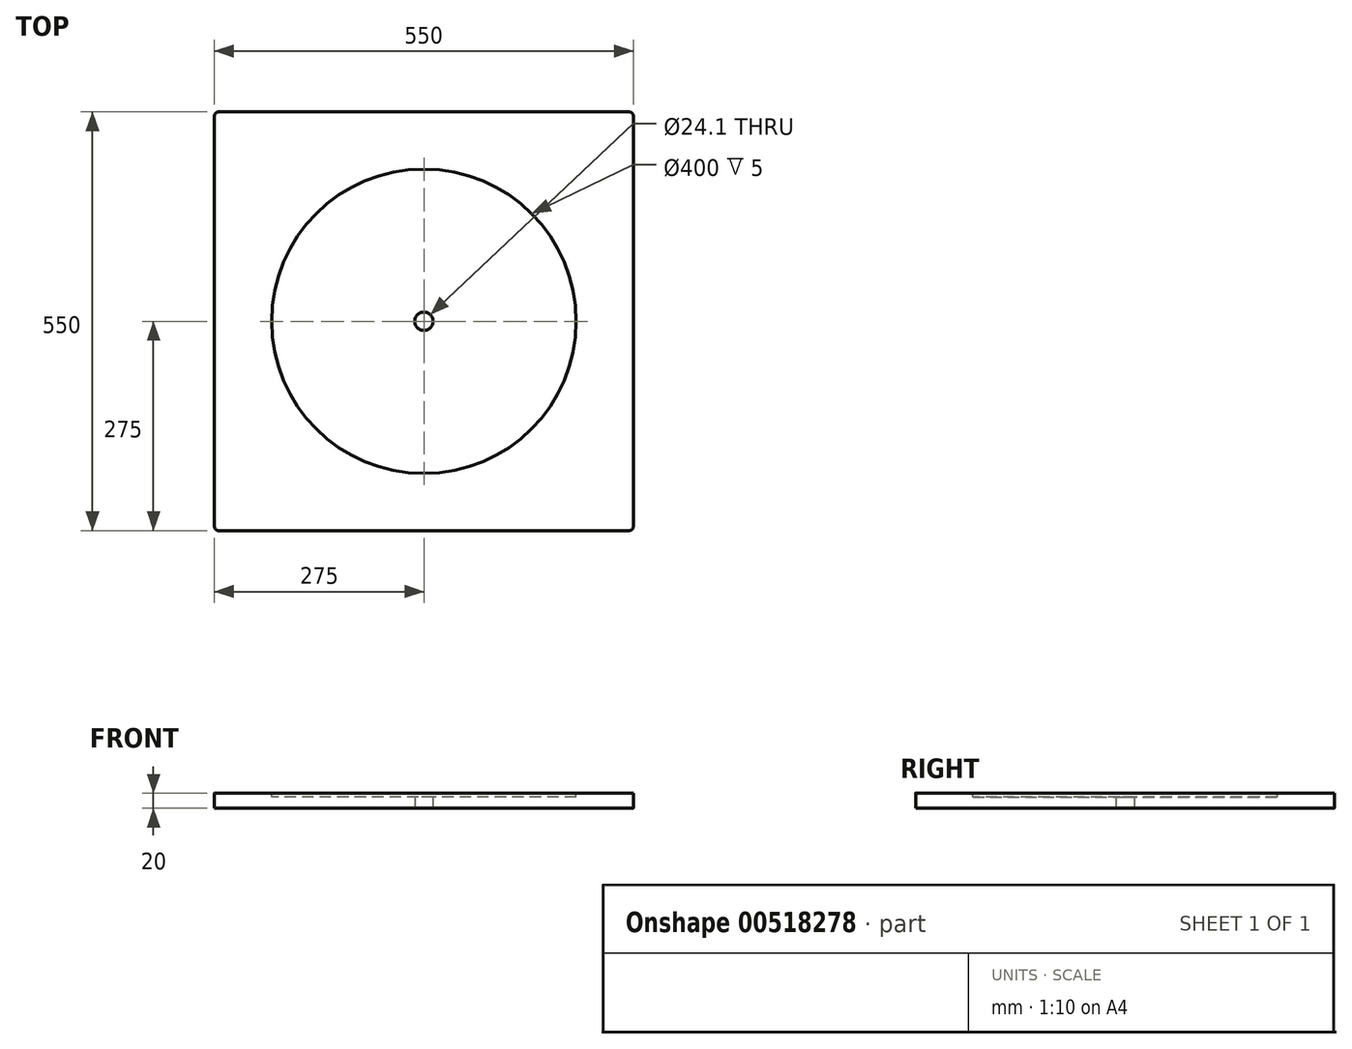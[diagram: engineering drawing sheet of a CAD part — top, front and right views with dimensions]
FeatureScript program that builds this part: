
annotation { "Feature Type Name" : "Feature", "Feature Type Description" : "" }
export const myFeature = defineFeature(function(context is Context, id is Id, definition is map)
    precondition{}
    {
        {
            var Q0;
            Q0=qCreatedBy(makeId("Top.planeOp"),FACE);
            var sketch = newSketch(context, id + "F0", { "sketchPlane" : qUnion([Q0])});
            skLineSegment(sketch, "E0.bottom", {"start": v(275, -275) * mm, "end": v(-275, -275) * mm});
            skLineSegment(sketch, "E0.top", {"start": v(275, 275) * mm, "end": v(-275, 275) * mm});
            skLineSegment(sketch, "E0.left", {"start": v(275, -275) * mm, "end": v(275, 275) * mm});
            skLineSegment(sketch, "E0.right", {"start": v(-275, -275) * mm, "end": v(-275, 275) * mm});
            skPoint(sketch, "E0.middle", {"position": v(0, 0) * mm});
            skCircle(sketch, "E1", {"center": v(0, 0) * mm, "radius": 12.05 * mm});
            skSolve(sketch);
        }
        {
            var Q0;
            Q0=makeQuery(id+"F0.imprint","IMPRINT",FACE,{"disambiguationData":[TD([[makeQuery(id+"F0.imprint","IMPRINT",EDGE,{"derivedFrom":sQuery(id+"F0.wireOp",EDGE,"E0.bottom")}),-1.0]])]});
            extrude(context, id + "F1", {"entities" : qUnion([Q0]), "depth" : 20 * mm, "offsetDistance" : 25 * mm});
        }
        {
            var Q0;
            Q0=makeQuery(id+"F1.opExtrude","SWEPT_EDGE",EDGE,{"disambiguationData":[OSD([sQuery(id+"F0.wireOp",EDGE,"E0.bottom"),sQuery(id+"F0.wireOp",EDGE,"E0.right")])]});
            var Q1;
            Q1=makeQuery(id+"F1.opExtrude","SWEPT_EDGE",EDGE,{"disambiguationData":[OSD([sQuery(id+"F0.wireOp",EDGE,"E0.bottom"),sQuery(id+"F0.wireOp",EDGE,"E0.left")])]});
            var Q2;
            Q2=makeQuery(id+"F1.opExtrude","SWEPT_EDGE",EDGE,{"disambiguationData":[OSD([sQuery(id+"F0.wireOp",EDGE,"E0.top"),sQuery(id+"F0.wireOp",EDGE,"E0.left")])]});
            var Q3;
            Q3=makeQuery(id+"F1.opExtrude","SWEPT_EDGE",EDGE,{"disambiguationData":[OSD([sQuery(id+"F0.wireOp",EDGE,"E0.top"),sQuery(id+"F0.wireOp",EDGE,"E0.right")])]});
            fillet(context, id + "F2", {"entities" : qUnion([Q0, Q1, Q2, Q3]), "radius" : 5 * mm, "tangentPropagation" : true, "allowEdgeOverflow" : false});
        }
        {
            var Q0;
            Q0=makeQuery(id+"F1.opExtrude","CAP_FACE",FACE,{"disambiguationData":[OSD([sQuery(id+"F0.wireOp",EDGE,"E0.bottom"),sQuery(id+"F0.wireOp",EDGE,"E0.top"),sQuery(id+"F0.wireOp",EDGE,"E0.left"),sQuery(id+"F0.wireOp",EDGE,"E0.right")])],"isStart":false});
            var sketch = newSketch(context, id + "F3", { "sketchPlane" : qUnion([Q0])});
            skCircle(sketch, "E2", {"center": v(0, 0) * mm, "radius": 200 * mm});
            skSolve(sketch);
        }
        {
            var Q0;
            Q0=qSketchRegion(id+"F3",true);
            extrude(context, id + "F4", {"entities" : qUnion([Q0]), "operationType" : NewBodyOperationType.REMOVE, "oppositeDirection" : true, "depth" : 5 * mm, "offsetDistance" : 25 * mm});
        }
    });
